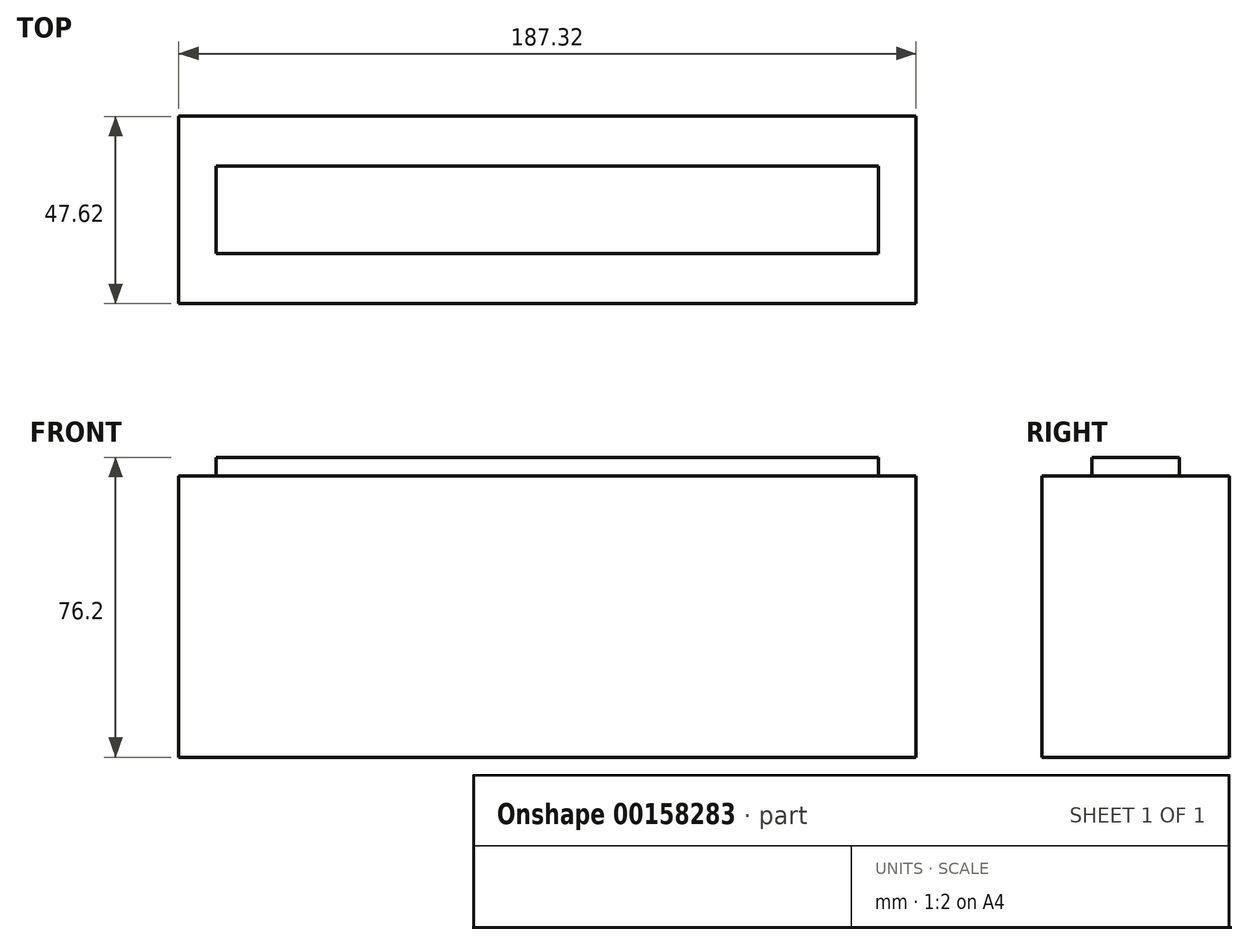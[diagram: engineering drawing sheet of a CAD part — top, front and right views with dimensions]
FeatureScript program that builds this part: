
annotation { "Feature Type Name" : "Feature", "Feature Type Description" : "" }
export const myFeature = defineFeature(function(context is Context, id is Id, definition is map)
    precondition{}
    {
        {
            var Q0;
            Q0=qCreatedBy(makeId("Top.planeOp"),FACE);
            var sketch = newSketch(context, id + "F0", { "sketchPlane" : qUnion([Q0])});
            skLineSegment(sketch, "E0.bottom", {"start": v(-4.76, -4.76) * mm, "end": v(182.56, -4.76) * mm});
            skLineSegment(sketch, "E0.top", {"start": v(-4.76, 42.86) * mm, "end": v(182.56, 42.86) * mm});
            skLineSegment(sketch, "E0.left", {"start": v(-4.76, -4.76) * mm, "end": v(-4.76, 42.86) * mm});
            skLineSegment(sketch, "E0.right", {"start": v(182.56, -4.76) * mm, "end": v(182.56, 42.86) * mm});
            skSolve(sketch);
        }
        {
            var Q0;
            Q0=makeQuery(id+"F0.imprint","IMPRINT",FACE,{"disambiguationData":[TD([[makeQuery(id+"F0.imprint","IMPRINT",EDGE,{"derivedFrom":sQuery(id+"F0.wireOp",EDGE,"E0.bottom")}),1.0]])]});
            extrude(context, id + "F1", {"entities" : qUnion([Q0]), "oppositeDirection" : true, "depth" : 76.2 * mm});
        }
        {
            var Q0;
            Q0=makeQuery(id+"F1.opExtrude","CAP_FACE",FACE,{"disambiguationData":[OSD([sQuery(id+"F0.wireOp",EDGE,"E0.bottom"),sQuery(id+"F0.wireOp",EDGE,"E0.top"),sQuery(id+"F0.wireOp",EDGE,"E0.left"),sQuery(id+"F0.wireOp",EDGE,"E0.right")])],"isStart":true});
            var sketch = newSketch(context, id + "F2", { "sketchPlane" : qUnion([Q0])});
            skLineSegment(sketch, "E1.bottom", {"start": v(-4.76, -4.76) * mm, "end": v(182.56, -4.76) * mm});
            skLineSegment(sketch, "E1.top", {"start": v(-4.76, 42.86) * mm, "end": v(182.56, 42.86) * mm});
            skLineSegment(sketch, "E1.left", {"start": v(-4.76, -4.76) * mm, "end": v(-4.76, 42.86) * mm});
            skLineSegment(sketch, "E1.right", {"start": v(182.56, -4.76) * mm, "end": v(182.56, 42.86) * mm});
            skPoint(sketch, "E2.visualSharp", {"position": v(-4.76, 42.86) * mm});
            skPoint(sketch, "E3.visualSharp", {"position": v(-4.76, -4.76) * mm});
            skPoint(sketch, "E4.visualSharp", {"position": v(182.56, -4.76) * mm});
            skPoint(sketch, "E5.visualSharp", {"position": v(182.56, 42.86) * mm});
            skLineSegment(sketch, "E6.bottom", {"start": v(4.76, 7.94) * mm, "end": v(173.04, 7.94) * mm});
            skLineSegment(sketch, "E6.top", {"start": v(4.76, 30.16) * mm, "end": v(173.04, 30.16) * mm});
            skLineSegment(sketch, "E6.left", {"start": v(4.76, 7.94) * mm, "end": v(4.76, 30.16) * mm});
            skLineSegment(sketch, "E6.right", {"start": v(173.04, 7.94) * mm, "end": v(173.04, 30.16) * mm});
            skSolve(sketch);
        }
        {
            var Q0;
            Q0=qSketchRegion(id+"F2",true);
            extrude(context, id + "F3", {"entities" : qUnion([Q0]), "operationType" : NewBodyOperationType.REMOVE, "oppositeDirection" : true, "depth" : 4.76 * mm});
        }
    });
